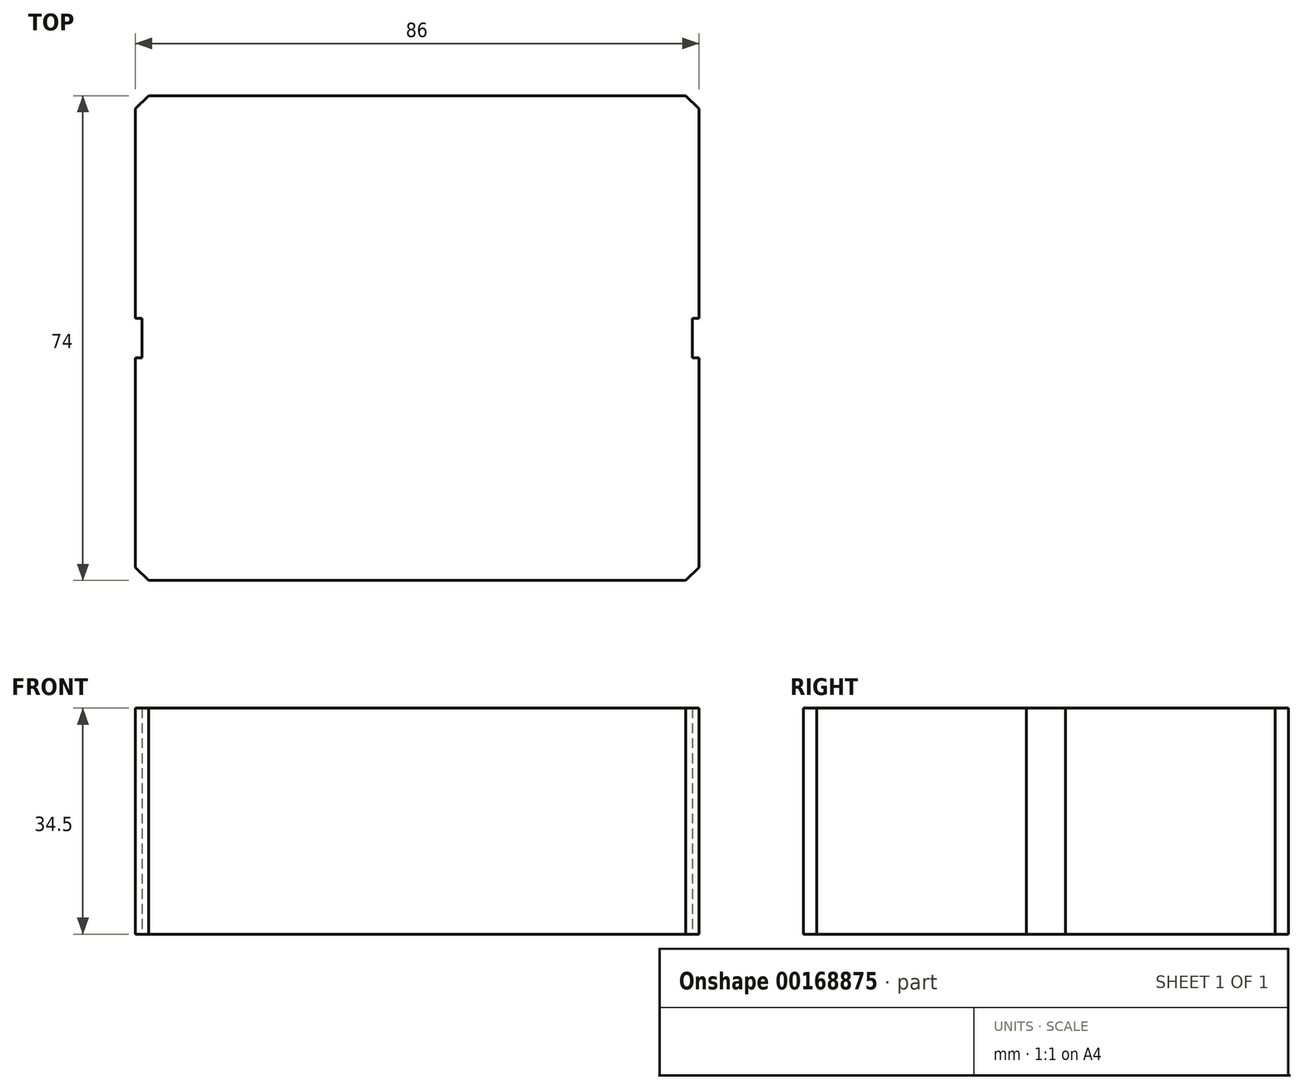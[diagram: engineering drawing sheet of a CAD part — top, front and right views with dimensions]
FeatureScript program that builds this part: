
annotation { "Feature Type Name" : "Feature", "Feature Type Description" : "" }
export const myFeature = defineFeature(function(context is Context, id is Id, definition is map)
    precondition{}
    {
        {
            var Q0;
            Q0=qCreatedBy(makeId("Top.planeOp"),FACE);
            var sketch = newSketch(context, id + "F0", { "sketchPlane" : qUnion([Q0])});
            skLineSegment(sketch, "E0.bottom", {"start": v(43, -37) * mm, "end": v(-43, -37) * mm});
            skLineSegment(sketch, "E0.top", {"start": v(43, 37) * mm, "end": v(-43, 37) * mm});
            skLineSegment(sketch, "E0.left", {"start": v(43, -37) * mm, "end": v(43, 37) * mm});
            skLineSegment(sketch, "E0.right", {"start": v(-43, -37) * mm, "end": v(-43, 37) * mm});
            skPoint(sketch, "E0.middle", {"position": v(0, 0) * mm});
            skLineSegment(sketch, "E1.bottom", {"start": v(43, 3) * mm, "end": v(42, 3) * mm});
            skLineSegment(sketch, "E1.top", {"start": v(43, -3) * mm, "end": v(42, -3) * mm});
            skLineSegment(sketch, "E1.left", {"start": v(43, 3) * mm, "end": v(43, -3) * mm});
            skLineSegment(sketch, "E1.right", {"start": v(42, 3) * mm, "end": v(42, -3) * mm});
            skLineSegment(sketch, "E2.MirrorCS", {"start": v(-42, 3) * mm, "end": v(-42, -3) * mm});
            skLineSegment(sketch, "E3.MirrorCS", {"start": v(-43, 3) * mm, "end": v(-42, 3) * mm});
            skLineSegment(sketch, "E4.MirrorCS", {"start": v(-43, 3) * mm, "end": v(-43, -3) * mm});
            skLineSegment(sketch, "E5.MirrorCS", {"start": v(-43, -3) * mm, "end": v(-42, -3) * mm});
            skSolve(sketch);
        }
        {
            var Q0;
            {var subQ1=sQuery(id+"F0.wireOp",EDGE,"E0.bottom");Q0=makeQuery(id+"F0.imprint","IMPRINT",FACE,{"disambiguationData":[TD([[makeQuery(id+"F0.imprint","IMPRINT",EDGE,{"derivedFrom":subQ1}),-1.0]])]});}
            extrude(context, id + "F1", {"entities" : qUnion([Q0]), "depth" : 34.5 * mm});
        }
        {
            var Q0;
            Q0=makeQuery(id+"F1.opExtrude","SWEPT_EDGE",EDGE,{"disambiguationData":[OSD([sQuery(id+"F0.wireOp",EDGE,"E0.top"),sQuery(id+"F0.wireOp",EDGE,"E0.left")])]});
            var Q1;
            Q1=makeQuery(id+"F1.opExtrude","SWEPT_EDGE",EDGE,{"disambiguationData":[OSD([sQuery(id+"F0.wireOp",EDGE,"E0.bottom"),sQuery(id+"F0.wireOp",EDGE,"E0.left")])]});
            var Q2;
            Q2=makeQuery(id+"F1.opExtrude","SWEPT_EDGE",EDGE,{"disambiguationData":[OSD([sQuery(id+"F0.wireOp",EDGE,"E0.top"),sQuery(id+"F0.wireOp",EDGE,"E0.right")])]});
            var Q3;
            Q3=makeQuery(id+"F1.opExtrude","SWEPT_EDGE",EDGE,{"disambiguationData":[OSD([sQuery(id+"F0.wireOp",EDGE,"E0.bottom"),sQuery(id+"F0.wireOp",EDGE,"E0.right")])]});
            chamfer(context, id + "F2", {"entities" : qUnion([Q0, Q1, Q2, Q3]), "width" : 2 * mm, "tangentPropagation" : true});
        }
    });
